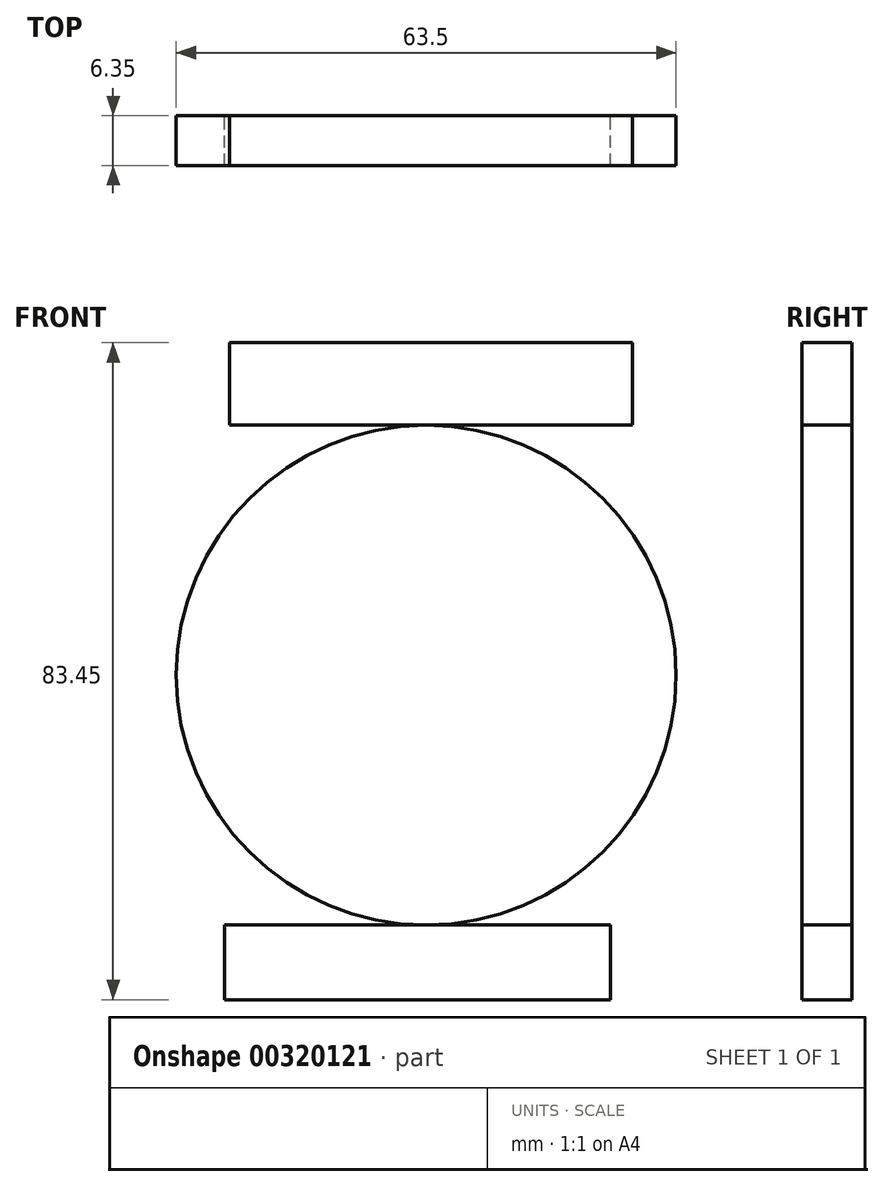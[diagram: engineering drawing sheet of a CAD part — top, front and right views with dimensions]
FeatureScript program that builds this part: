
annotation { "Feature Type Name" : "Feature", "Feature Type Description" : "" }
export const myFeature = defineFeature(function(context is Context, id is Id, definition is map)
    precondition{}
    {
        {
            var Q0;
            Q0=qCreatedBy(makeId("Front.planeOp"),FACE);
            var sketch = newSketch(context, id + "F0", { "sketchPlane" : qUnion([Q0])});
            skCircle(sketch, "E0", {"center": v(0, 0) * mm, "radius": 31.75 * mm});
            skLineSegment(sketch, "E1.bottom", {"start": v(-25, 42.23) * mm, "end": v(26.2, 42.23) * mm});
            skLineSegment(sketch, "E1.top", {"start": v(-25, 31.75) * mm, "end": v(26.2, 31.75) * mm});
            skLineSegment(sketch, "E1.left", {"start": v(-25, 42.23) * mm, "end": v(-25, 31.75) * mm});
            skLineSegment(sketch, "E1.right", {"start": v(26.2, 42.23) * mm, "end": v(26.2, 31.75) * mm});
            skLineSegment(sketch, "E2.bottom", {"start": v(-25.6, -31.75) * mm, "end": v(23.38, -31.75) * mm});
            skLineSegment(sketch, "E2.top", {"start": v(-25.6, -41.22) * mm, "end": v(23.38, -41.22) * mm});
            skLineSegment(sketch, "E2.left", {"start": v(-25.6, -31.75) * mm, "end": v(-25.6, -41.22) * mm});
            skLineSegment(sketch, "E2.right", {"start": v(23.38, -31.75) * mm, "end": v(23.38, -41.22) * mm});
            skSolve(sketch);
        }
        {
            var Q0;
            {var subQ0=sQuery(id+"F0.wireOp",EDGE,"E0");var subQ1=makeQuery(id+"F0.imprint","INTERSECT",VERTEX,{"derivedFrom":[subQ0,sQuery(id+"F0.wireOp",EDGE,"E1.top")]});Q0=makeQuery(id+"F0.imprint","IMPRINT",FACE,{"disambiguationData":[TD([[makeQuery(id+"F0.imprint","IMPRINT",EDGE,{"disambiguationData":[TD([[subQ1,-1.0]])],"derivedFrom":subQ0}),1.0]])]});}
            extrude(context, id + "F1", {"entities" : qUnion([Q0]), "depth" : 6.35 * mm});
        }
        {
            var Q0;
            Q0=makeQuery(id+"F0.imprint","IMPRINT",FACE,{"disambiguationData":[TD([[makeQuery(id+"F0.imprint","IMPRINT",EDGE,{"derivedFrom":sQuery(id+"F0.wireOp",EDGE,"E1.bottom")}),-1.0]])]});
            extrude(context, id + "F2", {"entities" : qUnion([Q0]), "operationType" : NewBodyOperationType.ADD, "depth" : 6.35 * mm});
        }
        {
            var Q0;
            Q0=makeQuery(id+"F0.imprint","IMPRINT",FACE,{"disambiguationData":[TD([[makeQuery(id+"F0.imprint","IMPRINT",EDGE,{"derivedFrom":sQuery(id+"F0.wireOp",EDGE,"E2.top")}),1.0]])]});
            extrude(context, id + "F3", {"entities" : qUnion([Q0]), "operationType" : NewBodyOperationType.ADD, "depth" : 6.35 * mm});
        }
    });
